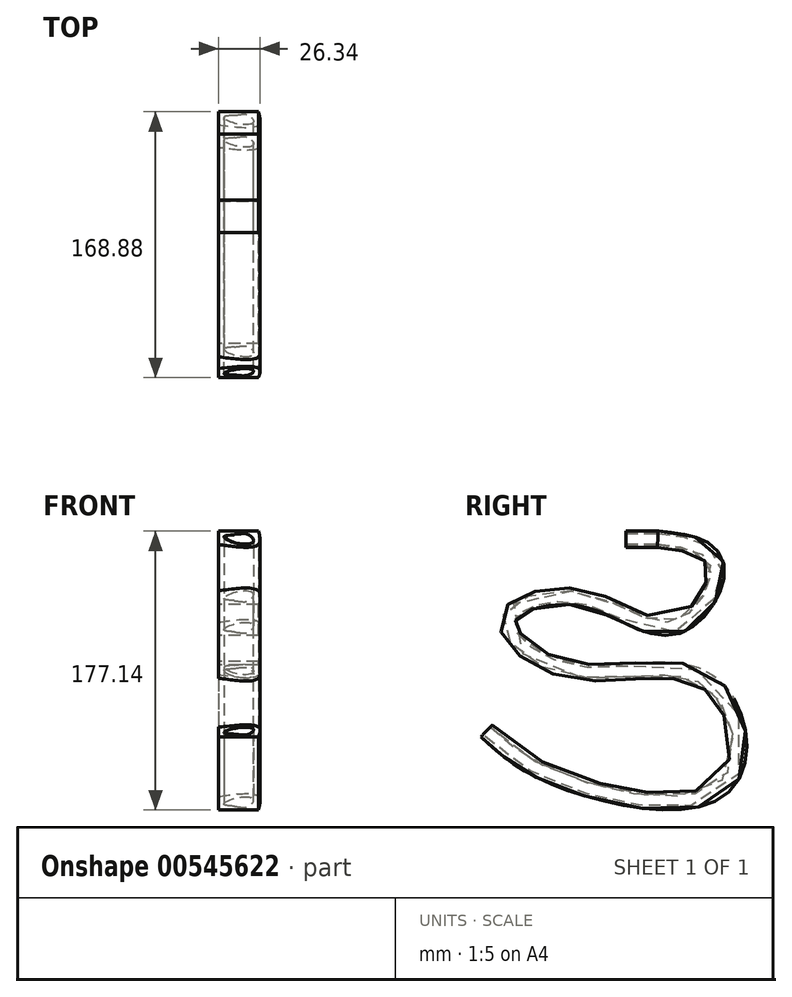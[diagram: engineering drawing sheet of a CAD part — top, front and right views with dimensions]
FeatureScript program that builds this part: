
annotation { "Feature Type Name" : "Feature", "Feature Type Description" : "" }
export const myFeature = defineFeature(function(context is Context, id is Id, definition is map)
    precondition{}
    {
        {
            var Q0;
            Q0=qCreatedBy(makeId("Front.planeOp"),FACE);
            var sketch = newSketch(context, id + "F0", { "sketchPlane" : qUnion([Q0])});
            skLineSegment(sketch, "E0.bottom", {"start": v(-60.23, 60.6) * mm, "end": v(-34.93, 60.6) * mm});
            skLineSegment(sketch, "E0.left", {"start": v(-60.23, 60.6) * mm, "end": v(-60.23, 52.04) * mm});
            skFitSpline(sketch, "E1", {"points": [v(-60.23, 52.04) * mm, v(-34.93, 52.04) * mm, v(-34.93, 60.6) * mm], "startDerivative": vector(52.67, -7.36) * mm, "endDerivative": vector(-7.36, 27.54) * mm});
            skPoint(sketch, "E2.orphan", {"position": v(-34.93, 43.48) * mm});
            skPoint(sketch, "E3.orphan", {"position": v(-60.23, 43.48) * mm});
            skFitSpline(sketch, "E4", {"points": [v(-50.05, 58.3) * mm, v(-56.78, 57.1) * mm, v(-50.5, 53.33) * mm, v(-38.24, 53.7) * mm, v(-41.1, 58.3) * mm, v(-50.05, 58.3) * mm]});
            skSolve(sketch);
        }
        {
            var Q0;
            Q0=qCreatedBy(makeId("Right.planeOp"),FACE);
            var sketch = newSketch(context, id + "F1", { "sketchPlane" : qUnion([Q0])});
            skLineSegment(sketch, "E5", {"start": v(0, 52.04) * mm, "end": v(20.05, 52.04) * mm});
            skFitSpline(sketch, "E6", {"points": [v(20.05, 52.04) * mm, v(53.53, 38.86) * mm, v(31.21, 3.64) * mm, v(-27.38, 21.42) * mm, v(-78.65, 5.03) * mm, v(-35.75, -31.24) * mm, v(50.4, -37.86) * mm, v(60.8, -97.74) * mm, v(-43.32, -92.53) * mm, v(-86.27, -63.9) * mm], "startDerivative": vector(535.59, -56.75) * mm, "endDerivative": vector(-304.46, 283.83) * mm});
            skSolve(sketch);
        }
        {
            var Q0;
            Q0 = qSketchRegion(id + "F0", true);
            var Q1;
            Q1 = qConstructionFilter(qBodyType(qCreatedBy(id + "F1" ,EDGE), BodyType.WIRE), ConstructionObject.NO);
            sweep(context, id + "F2", {"profiles" : qUnion([Q0]), "path" : qUnion([Q1])});
        }
    });
